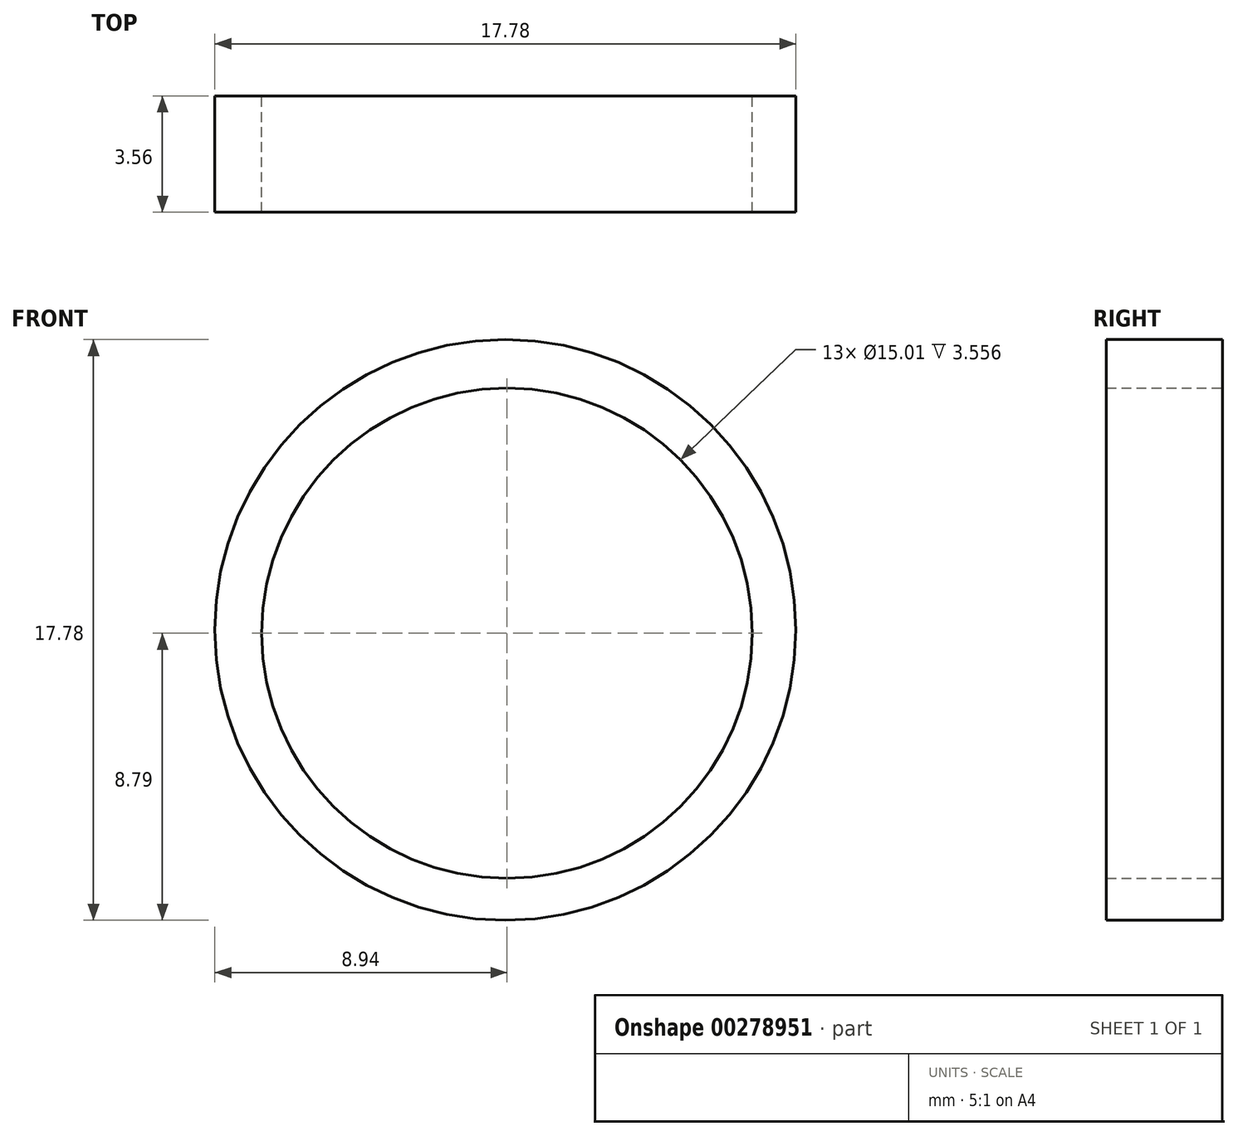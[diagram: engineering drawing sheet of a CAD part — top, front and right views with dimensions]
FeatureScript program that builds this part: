
annotation { "Feature Type Name" : "Feature", "Feature Type Description" : "" }
export const myFeature = defineFeature(function(context is Context, id is Id, definition is map)
    precondition{}
    {
        {
            var Q0;
            Q0=qCreatedBy(makeId("Front.planeOp"),FACE);
            var sketch = newSketch(context, id + "F0", { "sketchPlane" : qUnion([Q0])});
            skCircle(sketch, "E0", {"center": v(-0.05, 0.1) * mm, "radius": 8.9 * mm});
            skCircle(sketch, "E1", {"center": v(0, 0) * mm, "radius": 7.5 * mm});
            skLineSegment(sketch, "E2", {"start": v(0, 7.5) * mm, "end": v(0, 9) * mm});
            skLineSegment(sketch, "E3", {"start": v(-11.87, 11.06) * mm, "end": v(-12.5, 11.69) * mm});
            skLineSegment(sketch, "E4.MirrorCS", {"start": v(-4.54, 11.06) * mm, "end": v(-3.92, 11.69) * mm});
            skLineSegment(sketch, "E5", {"start": v(-3.92, 11.69) * mm, "end": v(-3.01, 10.8) * mm});
            skLineSegment(sketch, "E6.MirrorCS", {"start": v(-12.5, 11.69) * mm, "end": v(-13.4, 10.8) * mm});
            skLineSegment(sketch, "E7", {"start": v(-6.37, 9.22) * mm, "end": v(-10.04, 9.22) * mm});
            skLineSegment(sketch, "E8", {"start": v(-10.69, 9.87) * mm, "end": v(-5.73, 9.87) * mm});
            skLineSegment(sketch, "E9.trimOffspring", {"start": v(-5.73, 9.87) * mm, "end": v(-4.54, 11.06) * mm});
            skLineSegment(sketch, "E10.trimOffspring", {"start": v(-10.69, 9.87) * mm, "end": v(-11.87, 11.06) * mm});
            skPoint(sketch, "E11.MirrorCS.end.orphan", {"position": v(-9.1, 6.5) * mm});
            skPoint(sketch, "E11.MirrorCS.start.orphan", {"position": v(-8.2, 7.39) * mm});
            skLineSegment(sketch, "E12", {"start": v(-6.2, 7.6) * mm, "end": v(-3.01, 10.8) * mm});
            skPoint(sketch, "E13.start.orphan", {"position": v(-7.31, 6.5) * mm});
            skLineSegment(sketch, "E14", {"start": v(-7.73, 7.86) * mm, "end": v(-6.37, 9.22) * mm});
            skLineSegment(sketch, "E15", {"start": v(-8.68, 7.86) * mm, "end": v(-10.04, 9.22) * mm});
            skLineSegment(sketch, "E16", {"start": v(-10.21, 7.6) * mm, "end": v(-13.4, 10.8) * mm});
            skSolve(sketch);
        }
        {
            var Q0;
            Q0=makeQuery(id+"F0.imprint","IMPRINT",FACE,{"disambiguationData":[TD([[makeQuery(id+"F0.imprint","IMPRINT",EDGE,{"derivedFrom":sQuery(id+"F0.wireOp",EDGE,"E0")}),1.0]])]});
            extrude(context, id + "F1", {"entities" : qUnion([Q0]), "depth" : 3.56 * mm});
        }
    });
